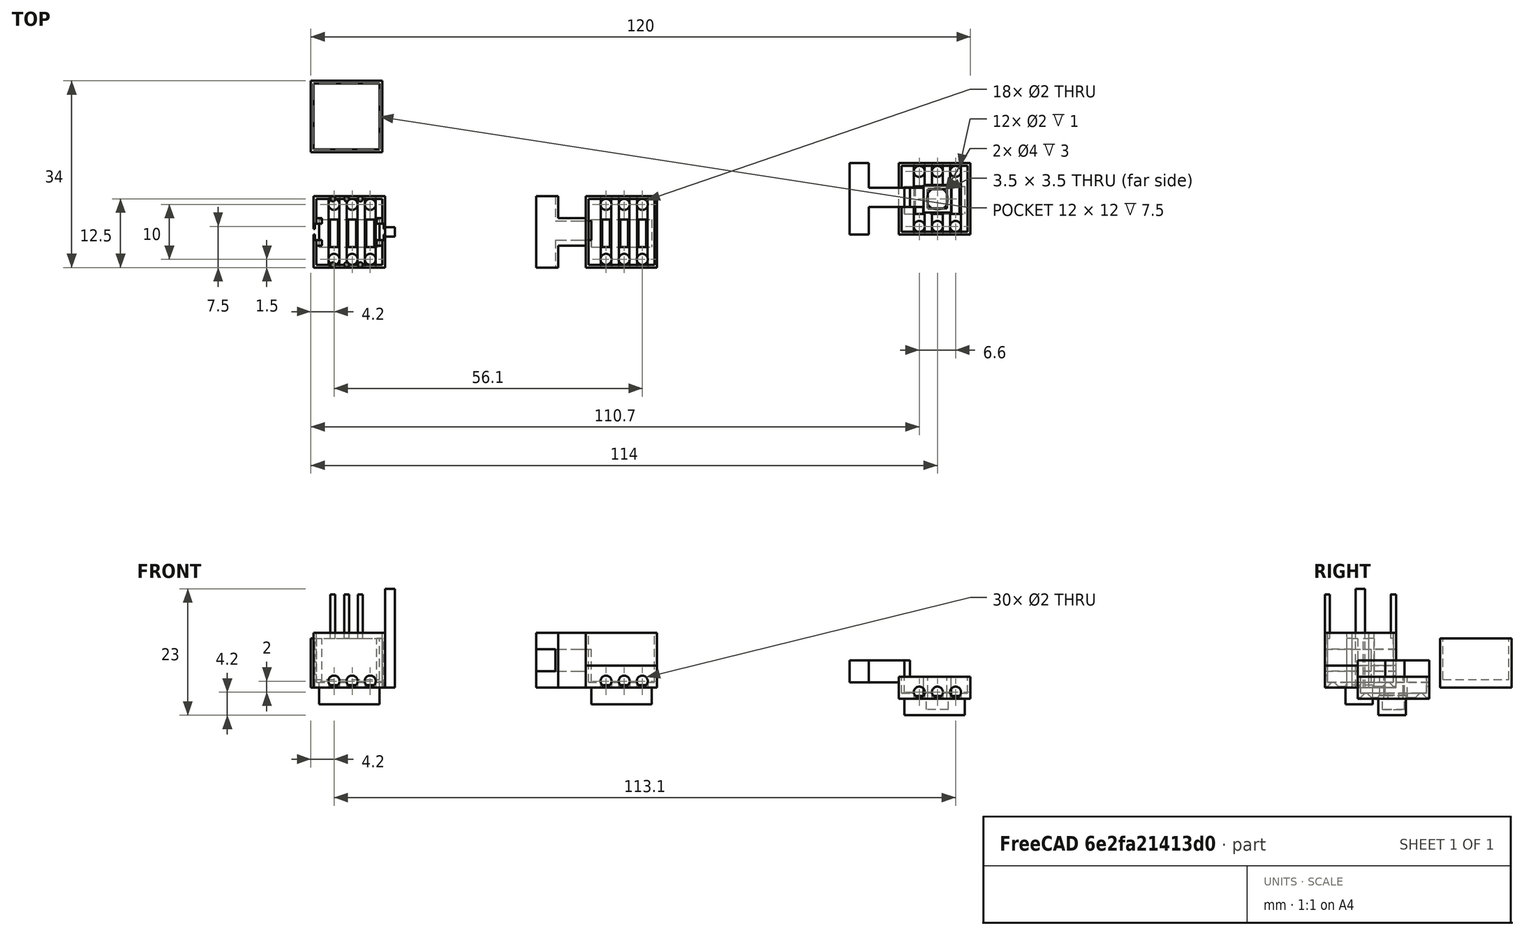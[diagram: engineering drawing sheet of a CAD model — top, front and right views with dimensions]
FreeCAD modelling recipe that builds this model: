
FCSTD DOCUMENT  (FreeCAD 0.19R24291 (Git))
Label: boton
License: All rights reserved
LicenseURL: http://en.wikipedia.org/wiki/All_rights_reserved
objects: Part::Box×40, Part::Cut×34, Part::MultiFuse×19, Part::Cylinder×16, Part::Feature×5, Part::Fuse×1
note: 115 computed .brp shape members not serialized (recipe doc carries the construction recipe); baked Part::Feature solids carry a one-line shape summary decoded from their .brp

FEATURE [Part::Box] Box  label="Cubo"
  AttacherType = Attacher::AttachEngine3D
  Height = 10
  Length = 13
  Width = 13
FEATURE [Part::Box] Box001  label="Cubo001"
  AttacherType = Attacher::AttachEngine3D
  Height = 9
  Length = 12
  Placement = pos=(0.5,0.5,1) rot=(0,0,1;0rad)
  Width = 12
FEATURE [Part::Cylinder] Cylinder001  label="Cilindro001"
  Angle = 360
  AttacherType = Attacher::AttachEngine3D
  Height = 20
  Placement = pos=(7,11.5,12.2) rot=(1,0,0;3.14159rad)
  Radius = 1
FEATURE [Part::Cylinder] Cylinder002  label="Cilindro002"
  Angle = 360
  AttacherType = Attacher::AttachEngine3D
  Height = 20
  Placement = pos=(10.3,11.5,12) rot=(1,0,0;3.14159rad)
  Radius = 1
FEATURE [Part::Cylinder] Cylinder003  label="Cilindro003"
  Angle = 360
  AttacherType = Attacher::AttachEngine3D
  Height = 20
  Placement = pos=(10.3,1.5,12) rot=(1,0,0;3.14159rad)
  Radius = 1
FEATURE [Part::Cylinder] Cylinder004  label="Cilindro004"
  Angle = 360
  AttacherType = Attacher::AttachEngine3D
  Height = 20
  Placement = pos=(3.7,1.5,12) rot=(1,0,0;3.14159rad)
  Radius = 1
FEATURE [Part::Cylinder] Cylinder005  label="Cilindro005"
  Angle = 360
  AttacherType = Attacher::AttachEngine3D
  Height = 20
  Placement = pos=(7,1.5,12) rot=(1,0,0;3.14159rad)
  Radius = 1
FEATURE [Part::Cylinder] Cylinder006  label="Cilindro006"
  Angle = 360
  AttacherType = Attacher::AttachEngine3D
  Height = 20
  Placement = pos=(10.3,17.7,1.2) rot=(1,0,0;1.5708rad)
  Radius = 1
FEATURE [Part::Cylinder] Cylinder007  label="Cilindro007"
  Angle = 360
  AttacherType = Attacher::AttachEngine3D
  Height = 20
  Placement = pos=(3.7,17,1.2) rot=(1,0,0;1.5708rad)
  Radius = 1
FEATURE [Part::Cylinder] Cylinder008  label="Cilindro008"
  Angle = 360
  AttacherType = Attacher::AttachEngine3D
  Height = 20
  Placement = pos=(7,17.7,1.2) rot=(1,0,0;1.5708rad)
  Radius = 1
FEATURE [Part::Box] Box002  label="Cubo002"
  AttacherType = Attacher::AttachEngine3D
  Height = 3.5
  Length = 11
  Placement = pos=(1,3.75,-3) rot=(0,0,1;0rad)
  Width = 5
FEATURE [Part::Cylinder] Cylinder  label="Cilindro"
  Angle = 360
  AttacherType = Attacher::AttachEngine3D
  Height = 20
  Placement = pos=(3.7,11.5,12) rot=(1,0,0;3.14159rad)
  Radius = 1
FEATURE [Part::Cut] Cut
  Base = -> Box
  Tool = -> Box001
FEATURE [Part::Cut] Cut001
  Base = -> Cut
  Tool = -> Cylinder002
FEATURE [Part::Cut] Cut002
  Base = -> Cut001
  Tool = -> Cylinder
FEATURE [Part::Cut] Cut003
  Base = -> Cut002
  Tool = -> Cylinder001
FEATURE [Part::Cut] Cut004
  Base = -> Cut003
  Tool = -> Cylinder005
FEATURE [Part::Cut] Cut005
  Base = -> Cut004
  Tool = -> Cylinder003
FEATURE [Part::Cut] Cut006
  Base = -> Cut005
  Tool = -> Cylinder004
FEATURE [Part::Cut] Cut007
  Base = -> Cut006
  Tool = -> Cylinder008
FEATURE [Part::Cut] Cut008
  Base = -> Cut007
  Tool = -> Cylinder006
FEATURE [Part::Cut] Cut009
  Base = -> Cut008
  Tool = -> Cylinder007
FEATURE [Part::Fuse] Fusion  label="Normal"
  Base = -> Box002
  Placement = pos=(50,0,0) rot=(0,0,1;0rad)
  Tool = -> Cut009
FEATURE [Part::Feature] Fusion_solid  label="Fusion (Solid)"
  shape: bbox 13 x 13 x 13 mm, 49 faces (baked)
FEATURE [Part::Cylinder] Cylinder009  label="Cilindro009"
  Angle = 360
  AttacherType = Attacher::AttachEngine3D
  Height = 8
  Placement = pos=(3.5,0.5,9) rot=(0,0,1;0rad)
  Radius = 0.45
FEATURE [Part::Cylinder] Cylinder010  label="Cilindro010"
  Angle = 360
  AttacherType = Attacher::AttachEngine3D
  Height = 8
  Placement = pos=(6,0.5,9) rot=(0,0,1;0rad)
  Radius = 0.45
FEATURE [Part::Cylinder] Cylinder011  label="Cilindro011"
  Angle = 360
  AttacherType = Attacher::AttachEngine3D
  Height = 8
  Placement = pos=(8.5,0.5,9) rot=(0,0,1;0rad)
  Radius = 0.45
FEATURE [Part::Cylinder] Cylinder012  label="Cilindro012"
  Angle = 360
  AttacherType = Attacher::AttachEngine3D
  Height = 8
  Placement = pos=(8.5,12.5,9) rot=(0,0,1;0rad)
  Radius = 0.45
FEATURE [Part::Cylinder] Cylinder013  label="Cilindro013"
  Angle = 360
  AttacherType = Attacher::AttachEngine3D
  Height = 8
  Placement = pos=(6,12.5,9) rot=(0,0,1;0rad)
  Radius = 0.45
FEATURE [Part::Cylinder] Cylinder014  label="Cilindro014"
  Angle = 360
  AttacherType = Attacher::AttachEngine3D
  Height = 8
  Placement = pos=(3.5,12.5,9) rot=(0,0,1;0rad)
  Radius = 0.45
FEATURE [Part::MultiFuse] Fusion001
  Shapes = -> [Fusion_solid,Cylinder009]
FEATURE [Part::MultiFuse] Fusion002
  Shapes = -> [Fusion001,Cylinder014]
FEATURE [Part::MultiFuse] Fusion003
  Shapes = -> [Cylinder013,Fusion002]
FEATURE [Part::MultiFuse] Fusion004
  Shapes = -> [Fusion003,Cylinder012]
FEATURE [Part::MultiFuse] Fusion005
  Shapes = -> [Fusion004,Cylinder011]
FEATURE [Part::MultiFuse] Fusion006  label="ConPatas"
  Shapes = -> [Fusion005,Cylinder010]
FEATURE [Part::Box] Box003  label="Cubo003"
  AttacherType = Attacher::AttachEngine3D
  Height = 9
  Length = 2
  Placement = pos=(-9,0,0) rot=(0,0,1;0rad)
  Width = 2
FEATURE [Part::Box] Box004  label="Cubo004"
  AttacherType = Attacher::AttachEngine3D
  Height = 10
  Length = 1
  Placement = pos=(-8,1,-0.5) rot=(0,0,1;0rad)
  Width = 1
FEATURE [Part::Cut] Cut010
  Base = -> Box003
  Placement = pos=(8,4,0) rot=(0,0,1;0rad)
  Tool = -> Box004
FEATURE [Part::Box] Box005  label="Cubo005"
  AttacherType = Attacher::AttachEngine3D
  Height = 10
  Length = 1
  Placement = pos=(-8,1,-0.5) rot=(0,0,1;0rad)
  Width = 1
FEATURE [Part::Box] Box006  label="Cubo006"
  AttacherType = Attacher::AttachEngine3D
  Height = 9
  Length = 2
  Placement = pos=(-9,0,0) rot=(0,0,1;0rad)
  Width = 2
FEATURE [Part::Cut] Cut011
  Base = -> Box006
  Placement = pos=(-1,0,0) rot=(0,0,-1;1.5708rad)
  Tool = -> Box005
FEATURE [Part::Box] Box007  label="Cubo007"
  AttacherType = Attacher::AttachEngine3D
  Height = 10
  Length = 1
  Placement = pos=(-8,1,-0.5) rot=(0,0,1;0rad)
  Width = 1
FEATURE [Part::Box] Box008  label="Cubo008"
  AttacherType = Attacher::AttachEngine3D
  Height = 9
  Length = 2
  Placement = pos=(-9,0,0) rot=(0,0,1;0rad)
  Width = 2
FEATURE [Part::Cut] Cut012
  Base = -> Box008
  Placement = pos=(14,13,0) rot=(0,0,1;1.5708rad)
  Tool = -> Box007
FEATURE [Part::Box] Box009  label="Cubo009"
  AttacherType = Attacher::AttachEngine3D
  Height = 10
  Length = 1
  Placement = pos=(-8,1,-0.5) rot=(0,0,1;0rad)
  Width = 1
FEATURE [Part::Box] Box010  label="Cubo010"
  AttacherType = Attacher::AttachEngine3D
  Height = 9
  Length = 2
  Placement = pos=(-9,0,0) rot=(0,0,1;0rad)
  Width = 2
FEATURE [Part::Cut] Cut013
  Base = -> Box010
  Placement = pos=(5,9,0) rot=(0,0,1;3.14159rad)
  Tool = -> Box009
FEATURE [Part::Box] Box011  label="Cubo011"
  AttacherType = Attacher::AttachEngine3D
  Height = 11
  Length = 1
  Placement = pos=(0,5,0) rot=(0,0,1;0rad)
  Width = 3
FEATURE [Part::Box] Box012  label="Cubo012"
  AttacherType = Attacher::AttachEngine3D
  Height = 11
  Length = 1
  Placement = pos=(12,5,0) rot=(0,0,1;0rad)
  Width = 3
FEATURE [Part::Cut] Cut014
  Base = -> Fusion006
  Tool = -> Box011
FEATURE [Part::Cut] Cut015
  Base = -> Cut014
  Placement = pos=(0.5,0,0) rot=(0,0,1;0rad)
  Tool = -> Box012
FEATURE [Part::Box] Box013  label="Cubo013"
  AttacherType = Attacher::AttachEngine3D
  Height = 10
  Length = 10
  Placement = pos=(13.5,0,0) rot=(0,0,1;0rad)
  Width = 10
FEATURE [Part::Cut] Cut016
  Base = -> Cut013
  Tool = -> Box013
FEATURE [Part::Box] Box014  label="Cubo014"
  AttacherType = Attacher::AttachEngine3D
  Height = 10
  Length = 10
  Placement = pos=(13.5,0,0) rot=(0,0,1;0rad)
  Width = 10
FEATURE [Part::Cut] Cut017
  Base = -> Cut012
  Tool = -> Box014
FEATURE [Part::Box] Box015  label="Cubo015"
  AttacherType = Attacher::AttachEngine3D
  Height = 10
  Length = 10
  Placement = pos=(-10.5,0,0) rot=(0,0,1;0rad)
  Width = 10
FEATURE [Part::Cut] Cut018
  Base = -> Cut010
  Placement = pos=(1,0,0) rot=(0,0,1;0rad)
  Tool = -> Box015
FEATURE [Part::Box] Box016  label="Cubo016"
  AttacherType = Attacher::AttachEngine3D
  Height = 10
  Length = 10
  Placement = pos=(-10.5,0,0) rot=(0,0,1;0rad)
  Width = 10
FEATURE [Part::Cut] Cut019
  Base = -> Cut011
  Placement = pos=(1,0,0) rot=(0,0,1;0rad)
  Tool = -> Box016
FEATURE [Part::MultiFuse] Fusion007
  Shapes = -> [Cut015,Cut016]
FEATURE [Part::MultiFuse] Fusion008
  Shapes = -> [Fusion007,Cut019]
FEATURE [Part::MultiFuse] Fusion009
  Shapes = -> [Fusion008,Cut018]
FEATURE [Part::MultiFuse] Fusion010  label="ConPatasyTopes"
  Shapes = -> [Fusion009,Cut017]
FEATURE [Part::Box] Box017  label="Cubo017"
  AttacherType = Attacher::AttachEngine3D
  Height = 9
  Length = 13
  Placement = pos=(0,21,0) rot=(0,0,1;0rad)
  Width = 13
FEATURE [Part::Box] Box018  label="Cubo018"
  AttacherType = Attacher::AttachEngine3D
  Height = 7.5
  Length = 12
  Placement = pos=(0.5,21.5,1.5) rot=(0,0,1;0rad)
  Width = 12
FEATURE [Part::Box] Box021  label="Cubo021"
  AttacherType = Attacher::AttachEngine3D
  Height = 18
  Length = 1.75
  Placement = pos=(13.5,5.6,0) rot=(0,0,1;0rad)
  Width = 1.75
FEATURE [Part::Box] Box022  label="Cubo022"
  AttacherType = Attacher::AttachEngine3D
  Height = 9
  Length = 0.75
  Placement = pos=(0.75,5,0) rot=(0,0,1;0rad)
  Width = 3
FEATURE [Part::Box] Box023  label="Cubo023"
  AttacherType = Attacher::AttachEngine3D
  Height = 9
  Length = 0.75
  Placement = pos=(12.5,5,0) rot=(0,0,1;0rad)
  Width = 3
FEATURE [Part::Cut] Cut021
  Base = -> Fusion010
  Tool = -> Box022
FEATURE [Part::Cut] Cut022
  Base = -> Cut021
  Tool = -> Box023
FEATURE [Part::MultiFuse] Fusion013  label="botonConTodo"
  Shapes = -> [Box021,Cut022]
FEATURE [Part::Box] Box024  label="Cubo024"
  AttacherType = Attacher::AttachEngine3D
  Height = 13
  Length = 8
  Width = 13
FEATURE [Part::Box] Box025  label="Cubo025"
  AttacherType = Attacher::AttachEngine3D
  Height = 17
  Length = 4
  Width = 4
FEATURE [Part::Box] Box026  label="Cubo026"
  AttacherType = Attacher::AttachEngine3D
  Height = 17
  Length = 4
  Placement = pos=(0,9,0) rot=(0,0,1;0rad)
  Width = 4
FEATURE [Part::Cut] Cut024
  Base = -> Box024
  Tool = -> Box025
FEATURE [Part::Cut] Cut025
  Base = -> Cut024
  Placement = pos=(50,13,0) rot=(0,0,1;3.14159rad)
  Tool = -> Box026
FEATURE [Part::Box] Box027  label="Cubo027"
  AttacherType = Attacher::AttachEngine3D
  Height = 10
  Length = 13
  Placement = pos=(38,-1,10) rot=(0,0,1;0rad)
  Width = 15
FEATURE [Part::Feature] Fusion_solid001  label="Normal (Solid)"
  shape: bbox 13 x 13 x 13 mm, 49 faces (baked)
FEATURE [Part::Cut] Cut026
  Base = -> Cut025
  Placement = pos=(-1,0,0) rot=(0,0,1;0rad)
  Tool = -> Box027
FEATURE [Part::Box] Box028  label="Cubo028"
  AttacherType = Attacher::AttachEngine3D
  Height = 10
  Length = 1
  Placement = pos=(49,4,0) rot=(0,0,1;0rad)
  Width = 5
FEATURE [Part::Box] Box029  label="Cubo029"
  AttacherType = Attacher::AttachEngine3D
  Height = 13
  Length = 5
  Placement = pos=(45,0,0) rot=(0,0,1;0rad)
  Width = 5
FEATURE [Part::Box] Box030  label="Cubo030"
  AttacherType = Attacher::AttachEngine3D
  Height = 13
  Length = 5
  Placement = pos=(45,8.5,0) rot=(0,0,1;0rad)
  Width = 5
FEATURE [Part::MultiFuse] Fusion014  label="tope"
  Shapes = -> [Cut026,Box028]
FEATURE [Part::Feature] Fusion014_solid  label="tope (Solid)"
  shape: bbox 9 x 13 x 10 mm, 14 faces (baked)
FEATURE [Part::Cut] Cut029  label="tapa"
  Base = -> Box017
  Tool = -> Box018
FEATURE [Part::Box] Box032  label="Cubo032"
  AttacherType = Attacher::AttachEngine3D
  Height = 10
  Length = 4
  Placement = pos=(44.5,0,0) rot=(0,0,1;0rad)
  Width = 5
FEATURE [Part::Box] Box033  label="Cubo033"
  AttacherType = Attacher::AttachEngine3D
  Height = 10
  Length = 4
  Placement = pos=(44.5,8.5,0) rot=(0,0,1;0rad)
  Width = 5
FEATURE [Part::MultiFuse] Fusion016
  Shapes = -> [Box029,Box032]
FEATURE [Part::MultiFuse] Fusion017
  Shapes = -> [Box030,Box033]
FEATURE [Part::Cut] Cut030
  Base = -> Fusion014_solid
  Tool = -> Fusion016
FEATURE [Part::Cut] Cut031
  Base = -> Cut030
  Tool = -> Fusion017
FEATURE [Part::Box] Box034  label="Cubo034"
  AttacherType = Attacher::AttachEngine3D
  Height = 10
  Length = 22
  Placement = pos=(41,-2,4) rot=(0,0,1;0rad)
  Width = 17
FEATURE [Part::Box] Box035  label="Cubo035"
  AttacherType = Attacher::AttachEngine3D
  Height = 10
  Length = 22
  Placement = pos=(41,-2,-7) rot=(0,0,1;0rad)
  Width = 17
FEATURE [Part::Cut] Cut032
  Base = -> Fusion_solid001
  Tool = -> Box034
FEATURE [Part::Box] Box036  label="Cubo036"
  AttacherType = Attacher::AttachEngine3D
  Height = 10
  Length = 22
  Placement = pos=(41,-3,7) rot=(0,0,1;0rad)
  Width = 17
FEATURE [Part::Cut] Cut033
  Base = -> Cut031
  Tool = -> Box035
FEATURE [Part::Cut] Cut034
  Base = -> Cut033
  Tool = -> Box036
FEATURE [Part::Box] Box037  label="Cubo037"
  AttacherType = Attacher::AttachEngine3D
  Height = 7
  Length = 1
  Placement = pos=(50,5,0) rot=(0,0,1;0rad)
  Width = 3.5
FEATURE [Part::MultiFuse] Fusion018
  Shapes = -> [Box037,Cut034]
FEATURE [Part::MultiFuse] Fusion019  label="botonTescalado"
  Shapes = -> [Cut032,Fusion018]
FEATURE [Part::Feature] Fusion019_solid  label="botonTescalado (Solid)"
  Placement = pos=(57,6,-2) rot=(0,0,1;0rad)
  shape: bbox 22 x 13 x 10 mm, 70 faces (baked)
FEATURE [Part::Cylinder] Cylinder015  label="Cilindro015"
  Angle = 360
  AttacherType = Attacher::AttachEngine3D
  Height = 10
  Placement = pos=(114,12.5,-4) rot=(0,0,1;0rad)
  Radius = 2
FEATURE [Part::Cut] Cut035
  Base = -> Fusion019_solid
  Tool = -> Cylinder015
FEATURE [Part::Box] Box038  label="Cubo038"
  AttacherType = Attacher::AttachEngine3D
  Height = 5
  Length = 3.5
  Placement = pos=(109.75,0.75,0) rot=(0,0,1;0rad)
  Width = 3.5
FEATURE [Part::Box] Box039  label="Cubo039"
  AttacherType = Attacher::AttachEngine3D
  Height = 5
  Length = 5
  Placement = pos=(109,0,0) rot=(0,0,1;0rad)
  Width = 5
FEATURE [Part::Cut] Cut036
  Base = -> Box039
  Placement = pos=(2.5,10,-2) rot=(0,0,1;0rad)
  Tool = -> Box038
FEATURE [Part::Box] Box040  label="Cubo040"
  AttacherType = Attacher::AttachEngine3D
  Height = 10
  Length = 10
  Placement = pos=(109,7,2) rot=(0,0,1;0rad)
  Width = 10
FEATURE [Part::Cut] Cut037
  Base = -> Cut036
  Tool = -> Box040
FEATURE [Part::MultiFuse] Fusion020  label="botonTconhueco"
  Shapes = -> [Cut035,Cut037]
FEATURE [Part::Feature] Fusion020_solid  label="botonTconhueco (Solid)"
  shape: bbox 22 x 13 x 10 mm, 96 faces (baked)
FEATURE [Part::Box] Box041  label="Cubo041"
  AttacherType = Attacher::AttachEngine3D
  Height = 4
  Length = 5
  Placement = pos=(107,11,-2) rot=(0,0,1;0rad)
  Width = 3.5
FEATURE [Part::Box] Box042  label="Cubo042"
  AttacherType = Attacher::AttachEngine3D
  Height = 7
  Length = 2
  Placement = pos=(107,11,-2) rot=(0,0,1;0rad)
  Width = 3.5
FEATURE [Part::MultiFuse] Fusion021
  Shapes = -> [Box041,Box042]
FEATURE [Part::MultiFuse] Fusion022  label="botonFinal"
  Shapes = -> [Fusion020_solid,Fusion021]
